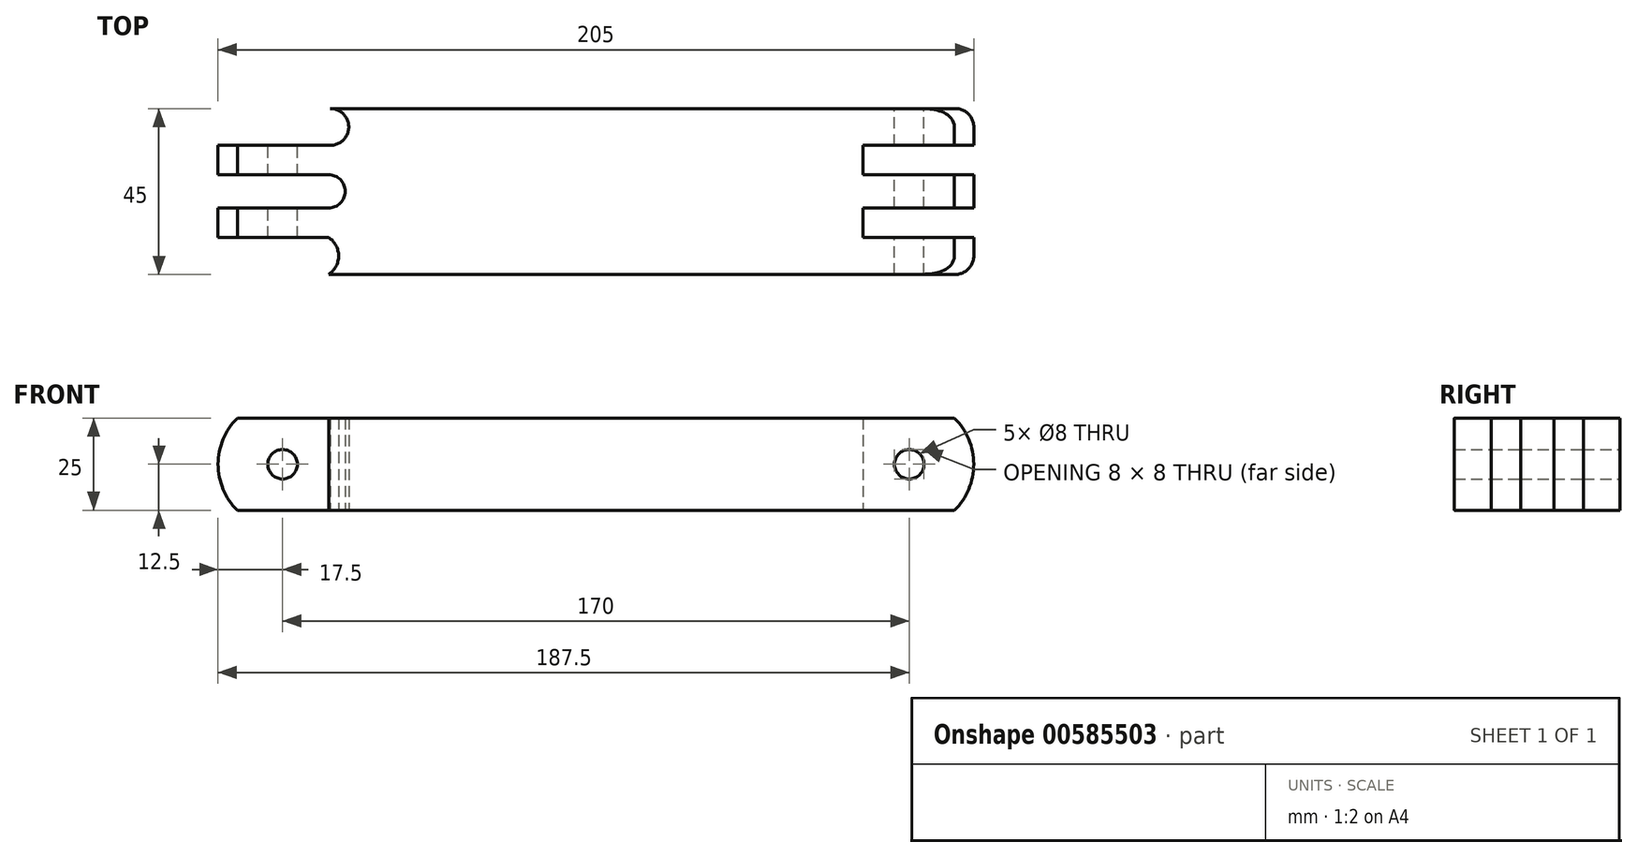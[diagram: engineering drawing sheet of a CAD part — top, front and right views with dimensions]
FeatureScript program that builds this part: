
annotation { "Feature Type Name" : "Feature", "Feature Type Description" : "" }
export const myFeature = defineFeature(function(context is Context, id is Id, definition is map)
    precondition{}
    {
        {
            var Q0;
            Q0=qCreatedBy(makeId("Front.planeOp"),FACE);
            var sketch = newSketch(context, id + "F0", { "sketchPlane" : qUnion([Q0])});
            skCircle(sketch, "E0", {"center": v(0, 0) * mm, "radius": 17.5 * mm});
            skCircle(sketch, "E1", {"center": v(170, 0) * mm, "radius": 17.5 * mm});
            skLineSegment(sketch, "E2", {"start": v(0, 0) * mm, "end": v(170, 0) * mm, "construction": true});
            skLineSegment(sketch, "E3", {"start": v(0, 17.5) * mm, "end": v(170, 17.5) * mm});
            skLineSegment(sketch, "E4.MirrorCS", {"start": v(0, -17.5) * mm, "end": v(170, -17.5) * mm});
            skCircle(sketch, "E5", {"center": v(0, 0) * mm, "radius": 4 * mm});
            skCircle(sketch, "E6", {"center": v(170, 0) * mm, "radius": 4 * mm});
            skSolve(sketch);
        }
        {
            var Q0;
            Q0=qSketchRegion(id+"F0",true);
            extrude(context, id + "F1", {"entities" : qUnion([Q0]), "depth" : 45 * mm, "offsetDistance" : 25 * mm});
        }
        {
            var Q0;
            Q0=qCreatedBy(makeId("Top.planeOp"),FACE);
            var sketch = newSketch(context, id + "F2", { "sketchPlane" : qUnion([Q0])});
            skLineSegment(sketch, "E7", {"start": v(157.5, -9.98) * mm, "end": v(187.5, -9.98) * mm});
            skLineSegment(sketch, "E8.0", {"start": v(157.5, -17.98) * mm, "end": v(187.5, -17.98) * mm});
            skLineSegment(sketch, "E9", {"start": v(187.5, -9.98) * mm, "end": v(187.5, -17.98) * mm});
            skLineSegment(sketch, "E10", {"start": v(187.5, 0) * mm, "end": v(187.5, -26.96) * mm});
            skLineSegment(sketch, "E11.0", {"start": v(202.2, 32.2) * mm, "end": v(-32.2, 32.2) * mm});
            skLineSegment(sketch, "E11.1", {"start": v(202.2, -77.2) * mm, "end": v(202.2, 32.2) * mm});
            skLineSegment(sketch, "E11.2", {"start": v(-32.2, -77.2) * mm, "end": v(202.2, -77.2) * mm});
            skLineSegment(sketch, "E11.3", {"start": v(-32.2, 32.2) * mm, "end": v(-32.2, -77.2) * mm});
            skLineSegment(sketch, "E12", {"start": v(157.5, -17.98) * mm, "end": v(157.5, -9.98) * mm});
            skLineSegment(sketch, "E13", {"start": v(187.5, -26.96) * mm, "end": v(157.5, -26.96) * mm});
            skLineSegment(sketch, "E14", {"start": v(157.5, -26.96) * mm, "end": v(157.5, -34.98) * mm});
            skLineSegment(sketch, "E15", {"start": v(157.5, -34.98) * mm, "end": v(187.5, -34.98) * mm});
            skLineSegment(sketch, "E16", {"start": v(187.5, -34.98) * mm, "end": v(187.5, -26.96) * mm});
            skLineSegment(sketch, "E17", {"start": v(-17.5, -45) * mm, "end": v(-17.5, 0) * mm});
            skLineSegment(sketch, "E18", {"start": v(-17.5, -34.98) * mm, "end": v(12.5, -34.98) * mm});
            skLineSegment(sketch, "E19", {"start": v(12.5, -45) * mm, "end": v(-17.5, -45) * mm});
            skLineSegment(sketch, "E20", {"start": v(-17.5, -26.96) * mm, "end": v(12.5, -26.96) * mm});
            skLineSegment(sketch, "E21", {"start": v(12.5, -26.96) * mm, "end": v(12.5, -17.98) * mm});
            skLineSegment(sketch, "E22", {"start": v(12.5, -17.98) * mm, "end": v(-17.5, -17.98) * mm});
            skLineSegment(sketch, "E23", {"start": v(-17.5, -17.98) * mm, "end": v(-17.5, -26.96) * mm});
            skLineSegment(sketch, "E24", {"start": v(-17.5, -9.98) * mm, "end": v(12.5, -9.98) * mm});
            skLineSegment(sketch, "E25", {"start": v(12.95, 0) * mm, "end": v(-17.5, 0) * mm});
            skLineSegment(sketch, "E26.0", {"start": v(0, 0) * mm, "end": v(170, 0) * mm});
            skLineSegment(sketch, "E27.0", {"start": v(0, -45) * mm, "end": v(170, -45) * mm});
            skPoint(sketch, "E28", {"position": v(85, 0) * mm});
            skLineSegment(sketch, "E29", {"start": v(85, 0) * mm, "end": v(85, -45) * mm, "construction": true});
            skPoint(sketch, "E30", {"position": v(85, -22.5) * mm});
            skArc(sketch, "E31", {"start": v(12.5, -45) * mm, "mid": v(15.2, -40) * mm, "end": v(12.5, -34.98) * mm});
            skArc(sketch, "E32", {"start": v(12.5, -26.96) * mm, "mid": v(16.99, -22.47) * mm, "end": v(12.5, -17.98) * mm});
            skArc(sketch, "E33", {"start": v(12.5, -9.98) * mm, "mid": v(17.94, -5.22) * mm, "end": v(12.95, 0) * mm});
            skSolve(sketch);
        }
        {
            var Q0;
            Q0=qSketchRegion(id+"F2",true);
            extrude(context, id + "F3", {"entities" : qUnion([Q0]), "operationType" : NewBodyOperationType.INTERSECT, "endBound" : BoundingType.SYMMETRIC, "depth" : 25 * mm, "offsetDistance" : 25 * mm});
        }
        {
            var Q0;
            Q0=makeQuery(id+"F3.boolean.opBoolean","INTERSECT",EDGE,{"derivedFrom":[makeQuery(id+"F1.opExtrude","CAP_FACE",FACE,{"disambiguationData":[OSD([sQuery(id+"F0.wireOp",EDGE,"E0"),sQuery(id+"F0.wireOp",EDGE,"E1"),sQuery(id+"F0.wireOp",EDGE,"E3"),sQuery(id+"F0.wireOp",EDGE,"E4.MirrorCS"),sQuery(id+"F0.wireOp",EDGE,"E5"),sQuery(id+"F0.wireOp",EDGE,"E6")])],"isStart":true}),makeQuery(id+"F3.boolean.toolComplement.opBoolean","COPY",FACE,{"derivedFrom":makeQuery(id+"F3.opExtrude","CAP_FACE",FACE,{"disambiguationData":[OSD([sQuery(id+"F2.wireOp",EDGE,"E7"),sQuery(id+"F2.wireOp",EDGE,"E8.0"),sQuery(id+"F2.wireOp",EDGE,"E10"),sQuery(id+"F2.wireOp",EDGE,"E11.0"),sQuery(id+"F2.wireOp",EDGE,"E11.1"),sQuery(id+"F2.wireOp",EDGE,"E11.2"),sQuery(id+"F2.wireOp",EDGE,"E11.3"),sQuery(id+"F2.wireOp",EDGE,"E12"),sQuery(id+"F2.wireOp",EDGE,"E13"),sQuery(id+"F2.wireOp",EDGE,"E14"),sQuery(id+"F2.wireOp",EDGE,"E15"),sQuery(id+"F2.wireOp",EDGE,"E16"),sQuery(id+"F2.wireOp",EDGE,"E17"),sQuery(id+"F2.wireOp",EDGE,"E18"),sQuery(id+"F2.wireOp",EDGE,"29Ro19xf-Q7Zu-ObNw-LcLb-FyusqM1WAvgB"),sQuery(id+"F2.wireOp",EDGE,"E19"),sQuery(id+"F2.wireOp",EDGE,"E20"),sQuery(id+"F2.wireOp",EDGE,"E21"),sQuery(id+"F2.wireOp",EDGE,"E22"),sQuery(id+"F2.wireOp",EDGE,"E23"),sQuery(id+"F2.wireOp",EDGE,"E24"),sQuery(id+"F2.wireOp",EDGE,"OmWtCRD3-Alp2-WJ4N-d6UF-zwBNbmMcEv39"),sQuery(id+"F2.wireOp",EDGE,"E25"),sQuery(id+"F2.wireOp",EDGE,"E26.0"),sQuery(id+"F2.wireOp",EDGE,"E27.0")])],"isStart":false})})]});
            var Q1;
            Q1=makeQuery(id+"F3.boolean.opBoolean","INTERSECT",EDGE,{"derivedFrom":[makeQuery(id+"F1.opExtrude","CAP_FACE",FACE,{"disambiguationData":[OSD([sQuery(id+"F0.wireOp",EDGE,"E0"),sQuery(id+"F0.wireOp",EDGE,"E1"),sQuery(id+"F0.wireOp",EDGE,"E3"),sQuery(id+"F0.wireOp",EDGE,"E4.MirrorCS"),sQuery(id+"F0.wireOp",EDGE,"E5"),sQuery(id+"F0.wireOp",EDGE,"E6")])],"isStart":false}),makeQuery(id+"F3.boolean.toolComplement.opBoolean","COPY",FACE,{"derivedFrom":makeQuery(id+"F3.opExtrude","CAP_FACE",FACE,{"disambiguationData":[OSD([sQuery(id+"F2.wireOp",EDGE,"E7"),sQuery(id+"F2.wireOp",EDGE,"E8.0"),sQuery(id+"F2.wireOp",EDGE,"E10"),sQuery(id+"F2.wireOp",EDGE,"E11.0"),sQuery(id+"F2.wireOp",EDGE,"E11.1"),sQuery(id+"F2.wireOp",EDGE,"E11.2"),sQuery(id+"F2.wireOp",EDGE,"E11.3"),sQuery(id+"F2.wireOp",EDGE,"E12"),sQuery(id+"F2.wireOp",EDGE,"E13"),sQuery(id+"F2.wireOp",EDGE,"E14"),sQuery(id+"F2.wireOp",EDGE,"E15"),sQuery(id+"F2.wireOp",EDGE,"E16"),sQuery(id+"F2.wireOp",EDGE,"E17"),sQuery(id+"F2.wireOp",EDGE,"E18"),sQuery(id+"F2.wireOp",EDGE,"29Ro19xf-Q7Zu-ObNw-LcLb-FyusqM1WAvgB"),sQuery(id+"F2.wireOp",EDGE,"E19"),sQuery(id+"F2.wireOp",EDGE,"E20"),sQuery(id+"F2.wireOp",EDGE,"E21"),sQuery(id+"F2.wireOp",EDGE,"E22"),sQuery(id+"F2.wireOp",EDGE,"E23"),sQuery(id+"F2.wireOp",EDGE,"E24"),sQuery(id+"F2.wireOp",EDGE,"OmWtCRD3-Alp2-WJ4N-d6UF-zwBNbmMcEv39"),sQuery(id+"F2.wireOp",EDGE,"E25"),sQuery(id+"F2.wireOp",EDGE,"E26.0"),sQuery(id+"F2.wireOp",EDGE,"E27.0")])],"isStart":false})})]});
            var Q2;
            Q2=makeQuery(id+"F3.boolean.opBoolean","INTERSECT",EDGE,{"derivedFrom":[makeQuery(id+"F1.opExtrude","CAP_FACE",FACE,{"disambiguationData":[OSD([sQuery(id+"F0.wireOp",EDGE,"E0"),sQuery(id+"F0.wireOp",EDGE,"E1"),sQuery(id+"F0.wireOp",EDGE,"E3"),sQuery(id+"F0.wireOp",EDGE,"E4.MirrorCS"),sQuery(id+"F0.wireOp",EDGE,"E5"),sQuery(id+"F0.wireOp",EDGE,"E6")])],"isStart":true}),makeQuery(id+"F3.boolean.toolComplement.opBoolean","COPY",FACE,{"derivedFrom":makeQuery(id+"F3.opExtrude","CAP_FACE",FACE,{"disambiguationData":[OSD([sQuery(id+"F2.wireOp",EDGE,"E7"),sQuery(id+"F2.wireOp",EDGE,"E8.0"),sQuery(id+"F2.wireOp",EDGE,"E10"),sQuery(id+"F2.wireOp",EDGE,"E11.0"),sQuery(id+"F2.wireOp",EDGE,"E11.1"),sQuery(id+"F2.wireOp",EDGE,"E11.2"),sQuery(id+"F2.wireOp",EDGE,"E11.3"),sQuery(id+"F2.wireOp",EDGE,"E12"),sQuery(id+"F2.wireOp",EDGE,"E13"),sQuery(id+"F2.wireOp",EDGE,"E14"),sQuery(id+"F2.wireOp",EDGE,"E15"),sQuery(id+"F2.wireOp",EDGE,"E16"),sQuery(id+"F2.wireOp",EDGE,"E17"),sQuery(id+"F2.wireOp",EDGE,"E18"),sQuery(id+"F2.wireOp",EDGE,"29Ro19xf-Q7Zu-ObNw-LcLb-FyusqM1WAvgB"),sQuery(id+"F2.wireOp",EDGE,"E19"),sQuery(id+"F2.wireOp",EDGE,"E20"),sQuery(id+"F2.wireOp",EDGE,"E21"),sQuery(id+"F2.wireOp",EDGE,"E22"),sQuery(id+"F2.wireOp",EDGE,"E23"),sQuery(id+"F2.wireOp",EDGE,"E24"),sQuery(id+"F2.wireOp",EDGE,"OmWtCRD3-Alp2-WJ4N-d6UF-zwBNbmMcEv39"),sQuery(id+"F2.wireOp",EDGE,"E25"),sQuery(id+"F2.wireOp",EDGE,"E26.0"),sQuery(id+"F2.wireOp",EDGE,"E27.0")])],"isStart":true})})]});
            var Q3;
            Q3=makeQuery(id+"F3.boolean.opBoolean","INTERSECT",EDGE,{"derivedFrom":[makeQuery(id+"F1.opExtrude","CAP_FACE",FACE,{"disambiguationData":[OSD([sQuery(id+"F0.wireOp",EDGE,"E0"),sQuery(id+"F0.wireOp",EDGE,"E1"),sQuery(id+"F0.wireOp",EDGE,"E3"),sQuery(id+"F0.wireOp",EDGE,"E4.MirrorCS"),sQuery(id+"F0.wireOp",EDGE,"E5"),sQuery(id+"F0.wireOp",EDGE,"E6")])],"isStart":false}),makeQuery(id+"F3.boolean.toolComplement.opBoolean","COPY",FACE,{"derivedFrom":makeQuery(id+"F3.opExtrude","CAP_FACE",FACE,{"disambiguationData":[OSD([sQuery(id+"F2.wireOp",EDGE,"E7"),sQuery(id+"F2.wireOp",EDGE,"E8.0"),sQuery(id+"F2.wireOp",EDGE,"E10"),sQuery(id+"F2.wireOp",EDGE,"E11.0"),sQuery(id+"F2.wireOp",EDGE,"E11.1"),sQuery(id+"F2.wireOp",EDGE,"E11.2"),sQuery(id+"F2.wireOp",EDGE,"E11.3"),sQuery(id+"F2.wireOp",EDGE,"E12"),sQuery(id+"F2.wireOp",EDGE,"E13"),sQuery(id+"F2.wireOp",EDGE,"E14"),sQuery(id+"F2.wireOp",EDGE,"E15"),sQuery(id+"F2.wireOp",EDGE,"E16"),sQuery(id+"F2.wireOp",EDGE,"E17"),sQuery(id+"F2.wireOp",EDGE,"E18"),sQuery(id+"F2.wireOp",EDGE,"29Ro19xf-Q7Zu-ObNw-LcLb-FyusqM1WAvgB"),sQuery(id+"F2.wireOp",EDGE,"E19"),sQuery(id+"F2.wireOp",EDGE,"E20"),sQuery(id+"F2.wireOp",EDGE,"E21"),sQuery(id+"F2.wireOp",EDGE,"E22"),sQuery(id+"F2.wireOp",EDGE,"E23"),sQuery(id+"F2.wireOp",EDGE,"E24"),sQuery(id+"F2.wireOp",EDGE,"OmWtCRD3-Alp2-WJ4N-d6UF-zwBNbmMcEv39"),sQuery(id+"F2.wireOp",EDGE,"E25"),sQuery(id+"F2.wireOp",EDGE,"E26.0"),sQuery(id+"F2.wireOp",EDGE,"E27.0")])],"isStart":true})})]});
            var Q4;
            Q4=makeQuery(id+"F1.opExtrude","CAP_EDGE",EDGE,{"disambiguationData":[OSD([sQuery(id+"F0.wireOp",EDGE,"E1")])],"isStart":true});
            var Q5;
            Q5=makeQuery(id+"F1.opExtrude","CAP_EDGE",EDGE,{"disambiguationData":[OSD([sQuery(id+"F0.wireOp",EDGE,"E1")])],"isStart":false});
            var Q6;
            Q6=makeQuery(id+"F3.boolean.opBoolean","COPY",EDGE,{"derivedFrom":makeQuery(id+"F3.boolean.toolComplement.opBoolean","COPY",EDGE,{"derivedFrom":makeQuery(id+"F3.opExtrude","SWEPT_EDGE",EDGE,{"disambiguationData":[OSD([sQuery(id+"F2.wireOp",EDGE,"29Ro19xf-Q7Zu-ObNw-LcLb-FyusqM1WAvgB"),sQuery(id+"F2.wireOp",EDGE,"E27.0")])]})})});
            var Q7;
            Q7=makeQuery(id+"F3.boolean.opBoolean","COPY",EDGE,{"derivedFrom":makeQuery(id+"F3.boolean.toolComplement.opBoolean","COPY",EDGE,{"derivedFrom":makeQuery(id+"F3.opExtrude","SWEPT_EDGE",EDGE,{"disambiguationData":[OSD([sQuery(id+"F2.wireOp",EDGE,"OmWtCRD3-Alp2-WJ4N-d6UF-zwBNbmMcEv39"),sQuery(id+"F2.wireOp",EDGE,"E26.0")])]})})});
            fillet(context, id + "F4", {"entities" : qUnion([Q0, Q1, Q2, Q3, Q4, Q5, Q6, Q7]), "radius" : 5 * mm, "tangentPropagation" : true, "allowEdgeOverflow" : false});
        }
    });
